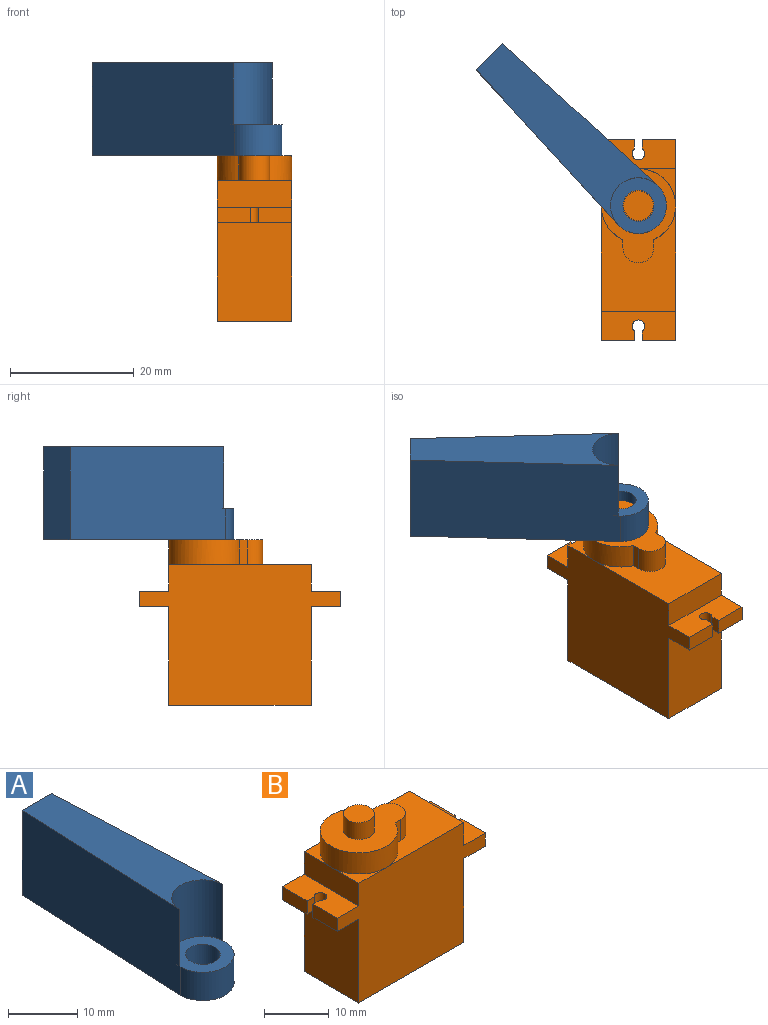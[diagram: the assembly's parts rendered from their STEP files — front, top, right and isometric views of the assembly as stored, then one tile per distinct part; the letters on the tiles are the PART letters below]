
ASSEMBLY  parts=2 mates=1
PART A: 9 faces, bbox 9x38.5x15 mm
  f0: plane 33.97x15mm, normal (-1,0.04,0), area 506mm2, adj f1,f3,f4,f5,f6,f8
  f1: cylinder r=4.5mm len=10mm, axis (0,0,-1), area 133.4mm2, adj f0,f2,f4,f8
  f2: plane 33.97x15mm, normal (1,0.04,0), area 506mm2, adj f1,f3,f4,f5,f6,f8
  f3: plane 15x6mm, normal (0,1,0), area 90mm2, adj f0,f2,f4,f5
  f4: plane 33.57x8.97mm, normal (0,0,1), area 222.9mm2, adj f0,f1,f2,f3
  f5: plane 38.47x9mm, normal (0,0,-1), area 266.9mm2, adj f0,f2,f3,f6,f7
  f6: cylinder r=4.5mm len=9mm, axis (0,0,-1), area 70.7mm2, adj f0,f2,f5,f8
  f7: cylinder r=2.5mm len=5mm, axis (0,0,-1), area 78.5mm2, adj f5,f8
  f8: plane 9x9mm, normal (0,0,1), area 44mm2, adj f0,f1,f2,f6,f7
PART B: 31 faces, bbox 32.4x12x29.9 mm
  f0: plane 5.35x2.5mm, normal (-1,0,0), area 13.4mm2, adj f9,f15,f16,f30
  f1: plane 5.35x2.5mm, normal (1,0,0), area 13.4mm2, adj f2,f3,f9,f27
  f2: plane 12x4.7mm, normal (0,0,-1), area 51.5mm2, adj f1,f6,f9,f11,f17,f25,f26,f27
  f3: plane 12x4.7mm, normal (0,0,1), area 51.5mm2, adj f1,f8,f9,f11,f17,f25,f26,f27
  f4: plane 17x12mm, normal (0,0,1), area 133.2mm2, adj f8,f9,f11,f18,f19,f20,f21
  f5: plane 6x6mm, normal (0,0,1), area 7.7mm2, adj f9,f10,f18
  f6: plane 15.9x12mm, normal (1,0,0), area 190.8mm2, adj f2,f9,f11,f13
  f7: plane 15.9x12mm, normal (-1,0,0), area 190.8mm2, adj f9,f11,f13,f15
  f8: plane 12x4.3mm, normal (1,0,0), area 51.6mm2, adj f3,f4,f9,f11
  f9: plane 32.4x22.7mm, normal (0,1,0), area 545.6mm2, adj f0,f1,f2,f3,f4,f5,f6,f7
  f10: plane 12x4.3mm, normal (-1,0,0), area 51.6mm2, adj f5,f9,f11,f12,f16
  f11: plane 32.4x22.7mm, normal (0,-1,0), area 545.6mm2, adj f2,f3,f4,f6,f7,f8,f10,f12
  f12: plane 6x6mm, normal (0,0,1), area 7.7mm2, adj f10,f11,f18
  f13: plane 23x12mm, normal (0,0,-1), area 276mm2, adj f6,f7,f9,f11
  f14: plane 5.35x2.5mm, normal (-1,0,0), area 13.4mm2, adj f11,f15,f16,f28
  f15: plane 12x4.7mm, normal (0,0,-1), area 51.5mm2, adj f0,f7,f9,f11,f14,f28,f29,f30
  f16: plane 12x4.7mm, normal (0,0,1), area 51.5mm2, adj f0,f9,f10,f11,f14,f28,f29,f30
  f17: plane 5.35x2.5mm, normal (1,0,0), area 13.4mm2, adj f2,f3,f11,f26
  f18: cylinder r=6mm len=12mm, axis (0,0,-1), area 130.2mm2, adj f4,f5,f12,f19,f21,f22
  f19: plane 4x1.25mm, normal (0,-1,0), area 5mm2, adj f4,f18,f20,f22
  f20: cylinder r=2.5mm len=5mm, axis (0,0,-1), area 31.4mm2, adj f4,f19,f21,f22
  f21: plane 4x1.25mm, normal (0,1,0), area 5mm2, adj f4,f18,f20,f22
  f22: plane 15.2x12mm, normal (0,0,1), area 109.2mm2, adj f18,f19,f20,f21,f23
  f23: cylinder r=2.4mm len=4.8mm, axis (0,0,-1), area 48.3mm2, adj f22,f24
  f24: plane 4.8x4.8mm, normal (0,0,1), area 18.1mm2, adj f23
  f25: cylinder r=1mm len=2.5mm, axis (0,0,1), area 12.2mm2, adj f2,f3,f26,f27
  f26: plane 2.5x1.54mm, normal (0,1,0), area 3.9mm2, adj f2,f3,f17,f25
  f27: plane 2.5x1.54mm, normal (0,-1,0), area 3.9mm2, adj f1,f2,f3,f25
  f28: plane 2.5x1.54mm, normal (0,1,0), area 3.9mm2, adj f14,f15,f16,f29
  f29: cylinder r=1mm len=2.5mm, axis (0,0,1), area 12.2mm2, adj f15,f16,f28,f30
  f30: plane 2.5x1.54mm, normal (0,-1,0), area 3.9mm2, adj f0,f15,f16,f29
PLACE A rot(axis=(0,0,1),45deg) t=(6,17,26.7)mm
PLACE B rot(axis=(0,0,-1),90deg) t=(6,11.5,0)mm fixed
MATE revolute A.f7 <-> B.f18  axis (0,0,-1) through (6,17,26.7)mm
